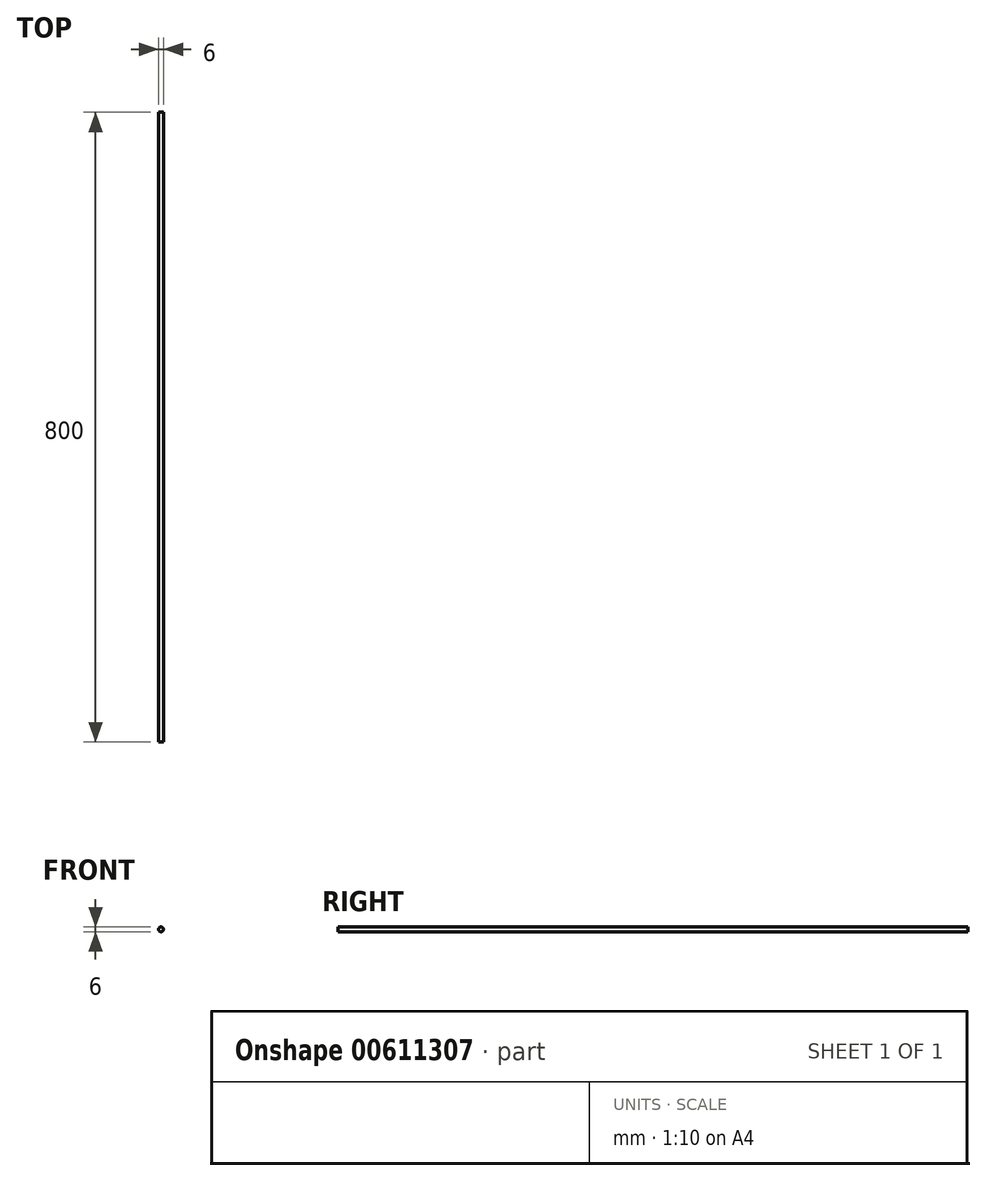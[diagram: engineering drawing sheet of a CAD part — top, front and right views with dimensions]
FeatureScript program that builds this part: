
annotation { "Feature Type Name" : "Feature", "Feature Type Description" : "" }
export const myFeature = defineFeature(function(context is Context, id is Id, definition is map)
    precondition{}
    {
        {
            var Q0;
            Q0=qCreatedBy(makeId("Front.planeOp"),FACE);
            var sketch = newSketch(context, id + "F0", { "sketchPlane" : qUnion([Q0])});
            skCircle(sketch, "E0", {"center": v(0, 0) * mm, "radius": 3 * mm});
            skSolve(sketch);
        }
        {
            var Q0;
            Q0=makeQuery(id+"F0.imprint","IMPRINT",FACE,{"disambiguationData":[TD([[makeQuery(id+"F0.imprint","IMPRINT",EDGE,{"derivedFrom":sQuery(id+"F0.wireOp",EDGE,"E0")}),1.0]])]});
            extrude(context, id + "F1", {"entities" : qUnion([Q0]), "depth" : 800 * mm, "offsetDistance" : 25.4 * mm});
        }
    });
